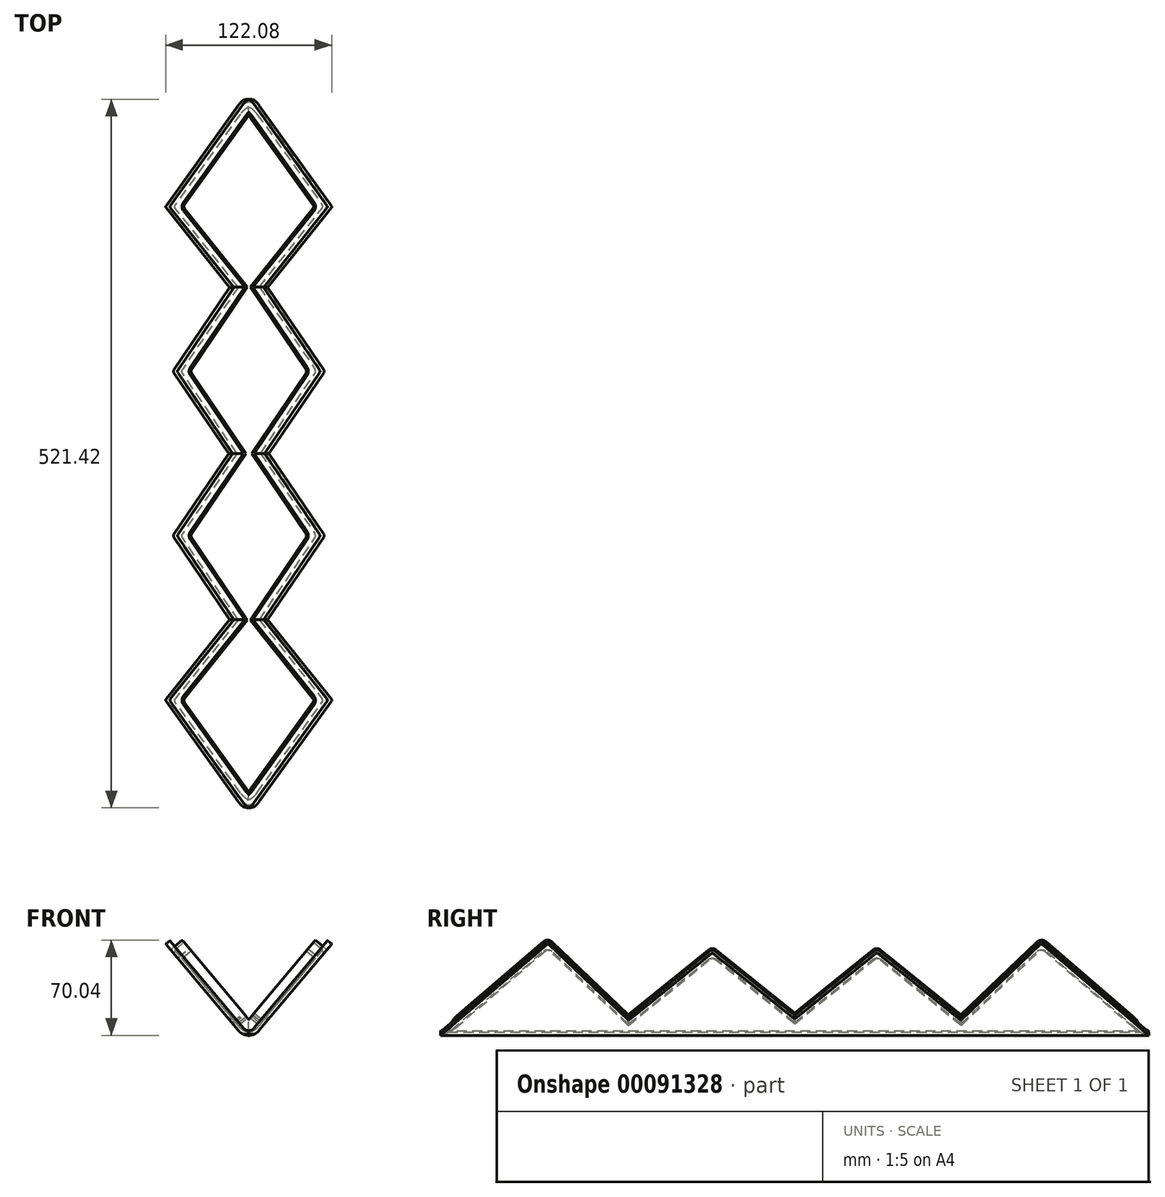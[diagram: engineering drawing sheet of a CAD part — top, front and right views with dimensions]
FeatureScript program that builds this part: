
annotation { "Feature Type Name" : "Feature", "Feature Type Description" : "" }
export const myFeature = defineFeature(function(context is Context, id is Id, definition is map)
    precondition{}
    {
        {
            var Q0;
            Q0=qCreatedBy(makeId("Right.planeOp"),FACE);
            var sketch = newSketch(context, id + "F0", { "sketchPlane" : qUnion([Q0])});
            skLineSegment(sketch, "E0", {"start": v(0, 0) * mm, "end": v(0, 95.5) * mm});
            skLineSegment(sketch, "E1", {"start": v(0, 95.5) * mm, "end": v(-77.94, 8.33) * mm});
            skLineSegment(sketch, "E2", {"start": v(0, 95.5) * mm, "end": v(76.78, 0) * mm});
            skLineSegment(sketch, "E3", {"start": v(-74.2, 0) * mm, "end": v(76.78, 0) * mm});
            skLineSegment(sketch, "E4", {"start": v(0, 0) * mm, "end": v(121, 0) * mm});
            skLineSegment(sketch, "E5", {"start": v(121, 0) * mm, "end": v(121, 86.8) * mm});
            skLineSegment(sketch, "E6", {"start": v(121, 86.8) * mm, "end": v(38.63, 0) * mm});
            skLineSegment(sketch, "E7", {"start": v(121, 0) * mm, "end": v(242, 0) * mm});
            skLineSegment(sketch, "E8", {"start": v(121, 86.8) * mm, "end": v(203.37, 0) * mm});
            skLineSegment(sketch, "E9", {"start": v(242, 0) * mm, "end": v(242, 86.8) * mm});
            skLineSegment(sketch, "E10", {"start": v(242, 0) * mm, "end": v(363, 0) * mm});
            skLineSegment(sketch, "E11", {"start": v(363, 0) * mm, "end": v(363, 95.5) * mm});
            skLineSegment(sketch, "E12", {"start": v(363, 95.5) * mm, "end": v(286.22, 0) * mm});
            skLineSegment(sketch, "E13", {"start": v(363, 95.5) * mm, "end": v(440.94, 8.33) * mm});
            skLineSegment(sketch, "E14", {"start": v(363, 0) * mm, "end": v(437.2, 0) * mm});
            skLineSegment(sketch, "E15", {"start": v(242, 86.8) * mm, "end": v(159.63, 0) * mm});
            skLineSegment(sketch, "E16", {"start": v(242, 86.8) * mm, "end": v(324.37, 0) * mm});
            skPoint(sketch, "E17.visualSharp", {"position": v(-85.39, 0) * mm});
            skArc(sketch, "E17.filletArc", {"start": v(-77.94, 8.33) * mm, "mid": v(-78.77, 2.96) * mm, "end": v(-74.2, 0) * mm});
            skPoint(sketch, "E18.visualSharp", {"position": v(448.39, 0) * mm});
            skArc(sketch, "E18.filletArc", {"start": v(437.2, 0) * mm, "mid": v(441.77, 2.96) * mm, "end": v(440.94, 8.33) * mm});
            skSolve(sketch);
        }
        {
            var Q0;
            Q0=qCreatedBy(makeId("Front.planeOp"),FACE);
            var sketch = newSketch(context, id + "F1", { "sketchPlane" : qUnion([Q0])});
            skLineSegment(sketch, "E19", {"start": v(7.66, 9.13) * mm, "end": v(128.56, 153.2) * mm});
            skLineSegment(sketch, "E20", {"start": v(-7.66, 9.13) * mm, "end": v(-128.56, 153.2) * mm});
            skLineSegment(sketch, "E21", {"start": v(128.56, 153.2) * mm, "end": v(125.5, 155.78) * mm});
            skLineSegment(sketch, "E22", {"start": v(-128.56, 153.2) * mm, "end": v(-125.5, 155.78) * mm});
            skLineSegment(sketch, "E23.trimOffspring", {"start": v(-3.83, 10.79) * mm, "end": v(-125.5, 155.78) * mm});
            skLineSegment(sketch, "E24.trimOffspring", {"start": v(3.83, 10.79) * mm, "end": v(125.5, 155.78) * mm});
            skPoint(sketch, "E25.visualSharp", {"position": v(0, 0) * mm});
            skArc(sketch, "E25.filletArc", {"start": v(-7.66, 9.13) * mm, "mid": v(0, 5.56) * mm, "end": v(7.66, 9.13) * mm});
            skPoint(sketch, "E26.visualSharp", {"position": v(0, 6.22) * mm});
            skArc(sketch, "E27.filletArc", {"start": v(-3.83, 10.79) * mm, "mid": v(0, 9) * mm, "end": v(3.83, 10.79) * mm});
            skSolve(sketch);
        }
        {
            var Q0;
            Q0 = qSketchRegion(id + "F0", true);
            extrude(context, id + "F2", {"entities" : qUnion([Q0]), "endBound" : BoundingType.SYMMETRIC, "depth" : 200 * mm});
        }
        {
            var Q0;
            Q0 = qSketchRegion(id + "F1", true);
            extrude(context, id + "F3", {"entities" : qUnion([Q0]), "endBound" : BoundingType.SYMMETRIC, "depth" : 1200 * mm});
        }
        {
            var Q0;
            Q0=makeQuery(id+"F2.opExtrude","SWEPT_BODY",BODY,{"disambiguationData":[OSD([sQuery(id+"F0.wireOp",EDGE,"E1"),sQuery(id+"F0.wireOp",EDGE,"E2"),sQuery(id+"F0.wireOp",EDGE,"E3"),sQuery(id+"F0.wireOp",EDGE,"E4"),sQuery(id+"F0.wireOp",EDGE,"E6"),sQuery(id+"F0.wireOp",EDGE,"E7"),sQuery(id+"F0.wireOp",EDGE,"E8"),sQuery(id+"F0.wireOp",EDGE,"E10"),sQuery(id+"F0.wireOp",EDGE,"E12"),sQuery(id+"F0.wireOp",EDGE,"E13"),sQuery(id+"F0.wireOp",EDGE,"E14"),sQuery(id+"F0.wireOp",EDGE,"E15"),sQuery(id+"F0.wireOp",EDGE,"E16"),sQuery(id+"F0.wireOp",EDGE,"E17.filletArc")])]});
            var Q1;
            Q1=sQuery(id+"F0.wireOp",EDGE,"E4");
            transform(context, id + "F4", {"entities" : qUnion([Q0]), "transformType" : TransformType.ROTATION, "transformAxis" : qUnion([Q1]), "angle" : 40 * degree, "makeCopy" : false});
        }
        {
            var Q0;
            Q0=makeQuery(id+"F2.opExtrude","SWEPT_BODY",BODY,{"disambiguationData":[OSD([sQuery(id+"F0.wireOp",EDGE,"E1"),sQuery(id+"F0.wireOp",EDGE,"E2"),sQuery(id+"F0.wireOp",EDGE,"E3"),sQuery(id+"F0.wireOp",EDGE,"E4"),sQuery(id+"F0.wireOp",EDGE,"E6"),sQuery(id+"F0.wireOp",EDGE,"E7"),sQuery(id+"F0.wireOp",EDGE,"E8"),sQuery(id+"F0.wireOp",EDGE,"E10"),sQuery(id+"F0.wireOp",EDGE,"E12"),sQuery(id+"F0.wireOp",EDGE,"E13"),sQuery(id+"F0.wireOp",EDGE,"E14"),sQuery(id+"F0.wireOp",EDGE,"E15"),sQuery(id+"F0.wireOp",EDGE,"E16"),sQuery(id+"F0.wireOp",EDGE,"E17.filletArc")])]});
            var Q1;
            Q1=sQuery(id+"F0.wireOp",EDGE,"E4");
            transform(context, id + "F5", {"entities" : qUnion([Q0]), "transformType" : TransformType.ROTATION, "transformAxis" : qUnion([Q1]), "angle" : 80 * degree, "oppositeDirection" : true, "makeCopy" : true});
        }
        {
            var Q0;
            Q0=makeQuery(id+"F2.opExtrude","SWEPT_BODY",BODY,{"disambiguationData":[OSD([sQuery(id+"F0.wireOp",EDGE,"E1"),sQuery(id+"F0.wireOp",EDGE,"E2"),sQuery(id+"F0.wireOp",EDGE,"E3"),sQuery(id+"F0.wireOp",EDGE,"E4"),sQuery(id+"F0.wireOp",EDGE,"E6"),sQuery(id+"F0.wireOp",EDGE,"E7"),sQuery(id+"F0.wireOp",EDGE,"E8"),sQuery(id+"F0.wireOp",EDGE,"E10"),sQuery(id+"F0.wireOp",EDGE,"E12"),sQuery(id+"F0.wireOp",EDGE,"E13"),sQuery(id+"F0.wireOp",EDGE,"E14"),sQuery(id+"F0.wireOp",EDGE,"E15"),sQuery(id+"F0.wireOp",EDGE,"E16"),sQuery(id+"F0.wireOp",EDGE,"E17.filletArc")])]});
            var Q1;
            Q1=makeQuery(id+"F5.opPattern","COPY",BODY,{"derivedFrom":makeQuery(id+"F2.opExtrude","SWEPT_BODY",BODY,{"disambiguationData":[OSD([sQuery(id+"F0.wireOp",EDGE,"E1"),sQuery(id+"F0.wireOp",EDGE,"E2"),sQuery(id+"F0.wireOp",EDGE,"E3"),sQuery(id+"F0.wireOp",EDGE,"E4"),sQuery(id+"F0.wireOp",EDGE,"E6"),sQuery(id+"F0.wireOp",EDGE,"E7"),sQuery(id+"F0.wireOp",EDGE,"E8"),sQuery(id+"F0.wireOp",EDGE,"E10"),sQuery(id+"F0.wireOp",EDGE,"E12"),sQuery(id+"F0.wireOp",EDGE,"E13"),sQuery(id+"F0.wireOp",EDGE,"E14"),sQuery(id+"F0.wireOp",EDGE,"E15"),sQuery(id+"F0.wireOp",EDGE,"E16"),sQuery(id+"F0.wireOp",EDGE,"E17.filletArc")])]}),"instanceName":"1"});
            var Q2;
            Q2=makeQuery(id+"F3.opExtrude","SWEPT_BODY",BODY,{"disambiguationData":[OSD([sQuery(id+"F1.wireOp",EDGE,"E19"),sQuery(id+"F1.wireOp",EDGE,"E20"),sQuery(id+"F1.wireOp",EDGE,"E21"),sQuery(id+"F1.wireOp",EDGE,"E22"),sQuery(id+"F1.wireOp",EDGE,"E23.trimOffspring"),sQuery(id+"F1.wireOp",EDGE,"E24.trimOffspring"),sQuery(id+"F1.wireOp",EDGE,"E25.filletArc"),sQuery(id+"F1.wireOp",EDGE,"E26.filletArc")])]});
            booleanBodies(context, id + "F6", {"operationType" : BooleanOperationType.INTERSECTION, "tools" : qUnion([Q0, Q1, Q2])});
        }
        {
            var Q0;
            Q0=makeQuery(id+"F5.opPattern","COPY",EDGE,{"derivedFrom":makeQuery(id+"F2.opExtrude","SWEPT_EDGE",EDGE,{"disambiguationData":[OSD([sQuery(id+"F0.wireOp",EDGE,"E11"),sQuery(id+"F0.wireOp",EDGE,"E12"),sQuery(id+"F0.wireOp",EDGE,"E13")])]}),"instanceName":"1"});
            var Q1;
            Q1=makeQuery(id+"F5.opPattern","COPY",EDGE,{"derivedFrom":makeQuery(id+"F2.opExtrude","SWEPT_EDGE",EDGE,{"disambiguationData":[OSD([sQuery(id+"F0.wireOp",EDGE,"E9"),sQuery(id+"F0.wireOp",EDGE,"E15"),sQuery(id+"F0.wireOp",EDGE,"E16")])]}),"instanceName":"1"});
            var Q2;
            Q2=makeQuery(id+"F5.opPattern","COPY",EDGE,{"derivedFrom":makeQuery(id+"F2.opExtrude","SWEPT_EDGE",EDGE,{"disambiguationData":[OSD([sQuery(id+"F0.wireOp",EDGE,"E5"),sQuery(id+"F0.wireOp",EDGE,"E6"),sQuery(id+"F0.wireOp",EDGE,"E8")])]}),"instanceName":"1"});
            var Q3;
            Q3=makeQuery(id+"F5.opPattern","COPY",EDGE,{"derivedFrom":makeQuery(id+"F2.opExtrude","SWEPT_EDGE",EDGE,{"disambiguationData":[OSD([sQuery(id+"F0.wireOp",EDGE,"E0"),sQuery(id+"F0.wireOp",EDGE,"E1"),sQuery(id+"F0.wireOp",EDGE,"E2")])]}),"instanceName":"1"});
            var Q4;
            Q4=makeQuery(id+"F2.opExtrude","SWEPT_EDGE",EDGE,{"disambiguationData":[OSD([sQuery(id+"F0.wireOp",EDGE,"E0"),sQuery(id+"F0.wireOp",EDGE,"E1"),sQuery(id+"F0.wireOp",EDGE,"E2")])]});
            var Q5;
            Q5=makeQuery(id+"F2.opExtrude","SWEPT_EDGE",EDGE,{"disambiguationData":[OSD([sQuery(id+"F0.wireOp",EDGE,"E5"),sQuery(id+"F0.wireOp",EDGE,"E6"),sQuery(id+"F0.wireOp",EDGE,"E8")])]});
            var Q6;
            Q6=makeQuery(id+"F2.opExtrude","SWEPT_EDGE",EDGE,{"disambiguationData":[OSD([sQuery(id+"F0.wireOp",EDGE,"E9"),sQuery(id+"F0.wireOp",EDGE,"E15"),sQuery(id+"F0.wireOp",EDGE,"E16")])]});
            var Q7;
            Q7=makeQuery(id+"F2.opExtrude","SWEPT_EDGE",EDGE,{"disambiguationData":[OSD([sQuery(id+"F0.wireOp",EDGE,"E11"),sQuery(id+"F0.wireOp",EDGE,"E12"),sQuery(id+"F0.wireOp",EDGE,"E13")])]});
            fillet(context, id + "F7", {"entities" : qUnion([Q0, Q1, Q2, Q3, Q4, Q5, Q6, Q7]), "radius" : 1 * mm, "tangentPropagation" : true, "allowEdgeOverflow" : false});
        }
        {
            var Q0;
            Q0=makeQuery(id+"F3.opExtrude","SWEPT_FACE",FACE,{"disambiguationData":[OSD([sQuery(id+"F1.wireOp",EDGE,"E24.trimOffspring")])]});
            var sketch = newSketch(context, id + "F8", { "sketchPlane" : qUnion([Q0])});
            skLineSegment(sketch, "E28.0", {"start": v(83.14, -1.24) * mm, "end": v(3.24, 88.12) * mm});
            skLineSegment(sketch, "E29.0", {"start": v(-59.13, 17.97) * mm, "end": v(-2.85, 87.96) * mm});
            skLineSegment(sketch, "E30.0", {"start": v(-59.13, 17.97) * mm, "end": v(-118.1, 80.11) * mm});
            skLineSegment(sketch, "E31.0", {"start": v(-181.5, 19.41) * mm, "end": v(-123.9, 80.11) * mm});
            skLineSegment(sketch, "E32.0", {"start": v(-181.5, 19.41) * mm, "end": v(-239.1, 80.11) * mm});
            skLineSegment(sketch, "E33.0", {"start": v(-303.87, 17.97) * mm, "end": v(-244.9, 80.11) * mm});
            skLineSegment(sketch, "E34.0", {"start": v(-303.87, 17.97) * mm, "end": v(-360.15, 87.96) * mm});
            skLineSegment(sketch, "E35.0", {"start": v(-446.14, -1.24) * mm, "end": v(-366.24, 88.12) * mm});
            skLineSegment(sketch, "E36.0", {"start": v(-443.32, -1.24) * mm, "end": v(-366.33, 84.87) * mm});
            skLineSegment(sketch, "E37.0", {"start": v(-304, 14.78) * mm, "end": v(-360.23, 84.71) * mm});
            skLineSegment(sketch, "E38.0", {"start": v(-304, 14.78) * mm, "end": v(-244.9, 77.06) * mm});
            skLineSegment(sketch, "E39.0", {"start": v(-181.5, 16.36) * mm, "end": v(-239.1, 77.06) * mm});
            skLineSegment(sketch, "E40.0", {"start": v(-181.5, 16.36) * mm, "end": v(-123.9, 77.06) * mm});
            skLineSegment(sketch, "E41.0", {"start": v(-59, 14.78) * mm, "end": v(-118.1, 77.06) * mm});
            skLineSegment(sketch, "E42.0", {"start": v(-59, 14.78) * mm, "end": v(-1.3, 86.55) * mm});
            skLineSegment(sketch, "E43.0", {"start": v(80.32, -1.24) * mm, "end": v(1.76, 86.63) * mm});
            skPoint(sketch, "E44.visualSharp", {"position": v(0.1, 91.64) * mm});
            skArc(sketch, "E44.filletArc", {"start": v(3.24, 88.12) * mm, "mid": v(0.16, 89.45) * mm, "end": v(-2.85, 87.96) * mm});
            skPoint(sketch, "E45.visualSharp", {"position": v(0.19, 88.4) * mm});
            skArc(sketch, "E45.filletArc", {"start": v(1.76, 86.63) * mm, "mid": v(0.21, 87.3) * mm, "end": v(-1.3, 86.55) * mm});
            skPoint(sketch, "E46.visualSharp", {"position": v(-121, 80.12) * mm});
            skArc(sketch, "E46.filletArc", {"start": v(-118.1, 77.06) * mm, "mid": v(-121, 78.3) * mm, "end": v(-123.9, 77.06) * mm});
            skPoint(sketch, "E47.visualSharp", {"position": v(-242, 80.12) * mm});
            skArc(sketch, "E47.filletArc", {"start": v(-239.1, 77.06) * mm, "mid": v(-242, 78.3) * mm, "end": v(-244.9, 77.06) * mm});
            skPoint(sketch, "E48.visualSharp", {"position": v(-363.19, 88.4) * mm});
            skArc(sketch, "E48.filletArc", {"start": v(-360.23, 84.71) * mm, "mid": v(-363.24, 86.2) * mm, "end": v(-366.33, 84.87) * mm});
            skPoint(sketch, "E49.visualSharp", {"position": v(-121, 83.17) * mm});
            skArc(sketch, "E49.filletArc", {"start": v(-118.1, 80.11) * mm, "mid": v(-121, 81.36) * mm, "end": v(-123.9, 80.11) * mm});
            skPoint(sketch, "E50.visualSharp", {"position": v(-242, 83.17) * mm});
            skArc(sketch, "E50.filletArc", {"start": v(-239.1, 80.11) * mm, "mid": v(-242, 81.36) * mm, "end": v(-244.9, 80.11) * mm});
            skPoint(sketch, "E51.visualSharp", {"position": v(-363.1, 91.64) * mm});
            skArc(sketch, "E51.filletArc", {"start": v(-360.15, 87.96) * mm, "mid": v(-363.16, 89.45) * mm, "end": v(-366.24, 88.12) * mm});
            skLineSegment(sketch, "E52", {"start": v(-446.14, -1.24) * mm, "end": v(83.14, -1.24) * mm});
            skSolve(sketch);
        }
        {
            var Q0;
            {var subQ0=sQuery(id+"F8.wireOp",EDGE,"E52");var subQ1=sQuery(id+"F8.wireOp",EDGE,"E36.0");var subQ2=makeQuery(id+"F8.imprint","INTERSECT",VERTEX,{"derivedFrom":[subQ1,subQ0]});Q0=makeQuery(id+"F8.imprint","IMPRINT",FACE,{"disambiguationData":[TD([[makeQuery(id+"F8.imprint","IMPRINT",EDGE,{"disambiguationData":[TD([[subQ2,-1.0]])],"derivedFrom":subQ0}),1.0]])]});}
            var Q1;
            {var subQ0=sQuery(id+"F8.wireOp",EDGE,"E52");var subQ1=sQuery(id+"F8.wireOp",EDGE,"E35.0");var subQ2=makeQuery(id+"F8.imprint","INTERSECT",VERTEX,{"derivedFrom":[subQ1,subQ0]});Q1=makeQuery(id+"F8.imprint","IMPRINT",FACE,{"disambiguationData":[TD([[makeQuery(id+"F8.imprint","IMPRINT",EDGE,{"disambiguationData":[TD([[subQ2,-1.0]])],"derivedFrom":subQ0}),1.0]])]});}
            var Q2;
            Q2=makeQuery(id+"F8.imprint","IMPRINT",FACE,{"disambiguationData":[TD([[makeQuery(id+"F8.imprint","IMPRINT",EDGE,{"derivedFrom":sQuery(id+"F8.wireOp",EDGE,"E29.0")}),-1.0]])]});
            var Q3;
            {var subQ0=sQuery(id+"F8.wireOp",EDGE,"E52");var subQ1=sQuery(id+"F8.wireOp",EDGE,"E28.0");var subQ2=makeQuery(id+"F8.imprint","INTERSECT",VERTEX,{"derivedFrom":[subQ1,subQ0]});Q3=makeQuery(id+"F8.imprint","IMPRINT",FACE,{"disambiguationData":[TD([[makeQuery(id+"F8.imprint","IMPRINT",EDGE,{"disambiguationData":[TD([[subQ2,1.0]])],"derivedFrom":subQ0}),1.0]])]});}
            var Q4;
            Q4=makeQuery(id+"F8.imprint","IMPRINT",FACE,{"disambiguationData":[TD([[makeQuery(id+"F8.imprint","IMPRINT",EDGE,{"derivedFrom":sQuery(id+"F8.wireOp",EDGE,"E37.0")}),1.0]])]});
            extrude(context, id + "F9", {"entities" : qUnion([Q0, Q1, Q2, Q3, Q4]), "endBound" : BoundingType.SYMMETRIC, "depth" : 200 * mm});
        }
        {
            var Q0;
            Q0=makeQuery(id+"F9.opExtrude","SWEPT_BODY",BODY,{"disambiguationData":[OSD([sQuery(id+"F8.wireOp",EDGE,"E36.0"),sQuery(id+"F8.wireOp",EDGE,"E37.0"),sQuery(id+"F8.wireOp",EDGE,"E38.0"),sQuery(id+"F8.wireOp",EDGE,"E39.0"),sQuery(id+"F8.wireOp",EDGE,"E40.0"),sQuery(id+"F8.wireOp",EDGE,"E41.0"),sQuery(id+"F8.wireOp",EDGE,"E42.0"),sQuery(id+"F8.wireOp",EDGE,"E43.0"),sQuery(id+"F8.wireOp",EDGE,"bMcOR1rm-Mvnn-Ac2E-meyw-J8fwcEbngexK")])]});
            var Q1;
            Q1=makeQuery(id+"F9.opExtrude","SWEPT_BODY",BODY,{"disambiguationData":[OSD([sQuery(id+"F1.wireOp",EDGE,"E24.trimOffspring"),sQuery(id+"F1.wireOp",EDGE,"E27.filletArc"),sQuery(id+"F8.wireOp",EDGE,"E28.0"),sQuery(id+"F8.wireOp",EDGE,"E29.0"),sQuery(id+"F8.wireOp",EDGE,"E30.0"),sQuery(id+"F8.wireOp",EDGE,"E31.0"),sQuery(id+"F8.wireOp",EDGE,"E32.0"),sQuery(id+"F8.wireOp",EDGE,"E33.0"),sQuery(id+"F8.wireOp",EDGE,"E34.0"),sQuery(id+"F8.wireOp",EDGE,"E35.0")])]});
            var Q2;
            Q2=makeQuery(id+"F3.opExtrude","SWEPT_FACE",FACE,{"disambiguationData":[OSD([sQuery(id+"F1.wireOp",EDGE,"E25.filletArc")])]});
            transform(context, id + "F10", {"entities" : qUnion([Q0, Q1]), "transformType" : TransformType.ROTATION, "transformAxis" : qUnion([Q2]), "angle" : 80 * degree, "oppositeDirection" : true, "makeCopy" : true});
        }
        {
            var Q0;
            Q0=makeQuery(id+"F10.opPattern","COPY",BODY,{"derivedFrom":makeQuery(id+"F9.opExtrude","SWEPT_BODY",BODY,{"disambiguationData":[OSD([sQuery(id+"F1.wireOp",EDGE,"E24.trimOffspring"),sQuery(id+"F1.wireOp",EDGE,"E27.filletArc"),sQuery(id+"F8.wireOp",EDGE,"E28.0"),sQuery(id+"F8.wireOp",EDGE,"E29.0"),sQuery(id+"F8.wireOp",EDGE,"E30.0"),sQuery(id+"F8.wireOp",EDGE,"E31.0"),sQuery(id+"F8.wireOp",EDGE,"E32.0"),sQuery(id+"F8.wireOp",EDGE,"E33.0"),sQuery(id+"F8.wireOp",EDGE,"E34.0"),sQuery(id+"F8.wireOp",EDGE,"E35.0")])]}),"instanceName":"1"});
            var Q1;
            Q1=makeQuery(id+"F9.opExtrude","SWEPT_BODY",BODY,{"disambiguationData":[OSD([sQuery(id+"F1.wireOp",EDGE,"E24.trimOffspring"),sQuery(id+"F1.wireOp",EDGE,"E27.filletArc"),sQuery(id+"F8.wireOp",EDGE,"E28.0"),sQuery(id+"F8.wireOp",EDGE,"E29.0"),sQuery(id+"F8.wireOp",EDGE,"E30.0"),sQuery(id+"F8.wireOp",EDGE,"E31.0"),sQuery(id+"F8.wireOp",EDGE,"E32.0"),sQuery(id+"F8.wireOp",EDGE,"E33.0"),sQuery(id+"F8.wireOp",EDGE,"E34.0"),sQuery(id+"F8.wireOp",EDGE,"E35.0")])]});
            booleanBodies(context, id + "F11", {"operationType" : BooleanOperationType.INTERSECTION, "tools" : qUnion([Q0, Q1])});
        }
        {
            var Q0;
            Q0=qCreatedBy(makeId("Front.planeOp"),FACE);
            var sketch = newSketch(context, id + "F12", { "sketchPlane" : qUnion([Q0])});
            skLineSegment(sketch, "E53.0", {"start": v(7.66, 9.44) * mm, "end": v(128.4, 153.34) * mm});
            skLineSegment(sketch, "E54.0", {"start": v(-7.66, 9.44) * mm, "end": v(-128.4, 153.34) * mm});
            skLineSegment(sketch, "E55.0", {"start": v(0, 17.11) * mm, "end": v(-120.13, 160.28) * mm});
            skLineSegment(sketch, "E56.0", {"start": v(0, 17.11) * mm, "end": v(120.13, 160.28) * mm});
            skLineSegment(sketch, "E57", {"start": v(-128.4, 153.34) * mm, "end": v(-120.13, 160.28) * mm});
            skLineSegment(sketch, "E58", {"start": v(128.4, 153.34) * mm, "end": v(120.13, 160.28) * mm});
            skPoint(sketch, "E59.visualSharp", {"position": v(0, 0.31) * mm});
            skArc(sketch, "E59.filletArc", {"start": v(-7.66, 9.44) * mm, "mid": v(0, 5.87) * mm, "end": v(7.66, 9.44) * mm});
            skSolve(sketch);
        }
        {
            var Q0;
            Q0 = qSketchRegion(id + "F12", true);
            extrude(context, id + "F13", {"entities" : qUnion([Q0]), "endBound" : BoundingType.SYMMETRIC, "depth" : 1000 * mm});
        }
        {
            var Q0;
            {var subQ0=makeQuery(id+"F9.opExtrude","SWEPT_BODY",BODY,{"disambiguationData":[OSD([sQuery(id+"F8.wireOp",EDGE,"E28.0"),sQuery(id+"F8.wireOp",EDGE,"E29.0"),sQuery(id+"F8.wireOp",EDGE,"E30.0"),sQuery(id+"F8.wireOp",EDGE,"E31.0"),sQuery(id+"F8.wireOp",EDGE,"E32.0"),sQuery(id+"F8.wireOp",EDGE,"E33.0"),sQuery(id+"F8.wireOp",EDGE,"E34.0"),sQuery(id+"F8.wireOp",EDGE,"E35.0"),sQuery(id+"F8.wireOp",EDGE,"8uEF9ZhR-iFz6-4wNc-omvh-xYUL6ONzQTi8"),sQuery(id+"F8.wireOp",EDGE,"SOrMnbwB-VD1V-YOIJ-9Ikj-L4d8KCUjtkFe"),sQuery(id+"F8.wireOp",EDGE,"bMcOR1rm-Mvnn-Ac2E-meyw-J8fwcEbngexK")])]});Q0=makeQuery(id+"F11.opBoolean","INTERSECT",BODY,{"derivedFrom":[subQ0,makeQuery(id+"F10.opPattern","COPY",BODY,{"derivedFrom":subQ0,"instanceName":"1"})]});}
            var Q1;
            Q1=makeQuery(id+"F13.opExtrude","SWEPT_BODY",BODY,{"disambiguationData":[OSD([sQuery(id+"F12.wireOp",EDGE,"E53.0"),sQuery(id+"F12.wireOp",EDGE,"E54.0"),sQuery(id+"F12.wireOp",EDGE,"E55.0"),sQuery(id+"F12.wireOp",EDGE,"E56.0"),sQuery(id+"F12.wireOp",EDGE,"E57"),sQuery(id+"F12.wireOp",EDGE,"E58"),sQuery(id+"F12.wireOp",EDGE,"E59.filletArc")])]});
            booleanBodies(context, id + "F14", {"operationType" : BooleanOperationType.INTERSECTION, "tools" : qUnion([Q0, Q1])});
        }
        {
            var Q0;
            Q0=makeQuery(id+"F13.opExtrude","SWEPT_FACE",FACE,{"disambiguationData":[OSD([sQuery(id+"F12.wireOp",EDGE,"E56.0")])]});
            var Q1;
            Q1=makeQuery(id+"F13.opExtrude","SWEPT_FACE",FACE,{"disambiguationData":[OSD([sQuery(id+"F12.wireOp",EDGE,"E55.0")])]});
            shell(context, id + "F15", {"entities" : qUnion([Q0, Q1]), "thickness" : 2.1 * mm});
        }
        {
            var Q0;
            {var subQ0=makeQuery(id+"F9.opExtrude","SWEPT_FACE",FACE,{"disambiguationData":[OSD([sQuery(id+"F8.wireOp",EDGE,"E28.0")])]});Q0=makeQuery(id+"F11.opBoolean","INTERSECT",EDGE,{"derivedFrom":[subQ0,makeQuery(id+"F10.opPattern","COPY",FACE,{"derivedFrom":subQ0,"instanceName":"1"})]});}
            var Q1;
            {var subQ0=makeQuery(id+"F9.opExtrude","SWEPT_FACE",FACE,{"disambiguationData":[OSD([sQuery(id+"F8.wireOp",EDGE,"E35.0")])]});Q1=makeQuery(id+"F11.opBoolean","INTERSECT",EDGE,{"derivedFrom":[subQ0,makeQuery(id+"F10.opPattern","COPY",FACE,{"derivedFrom":subQ0,"instanceName":"1"})]});}
            fillet(context, id + "F16", {"entities" : qUnion([Q0, Q1]), "radius" : 5 * mm, "tangentPropagation" : true, "allowEdgeOverflow" : false});
        }
    });
